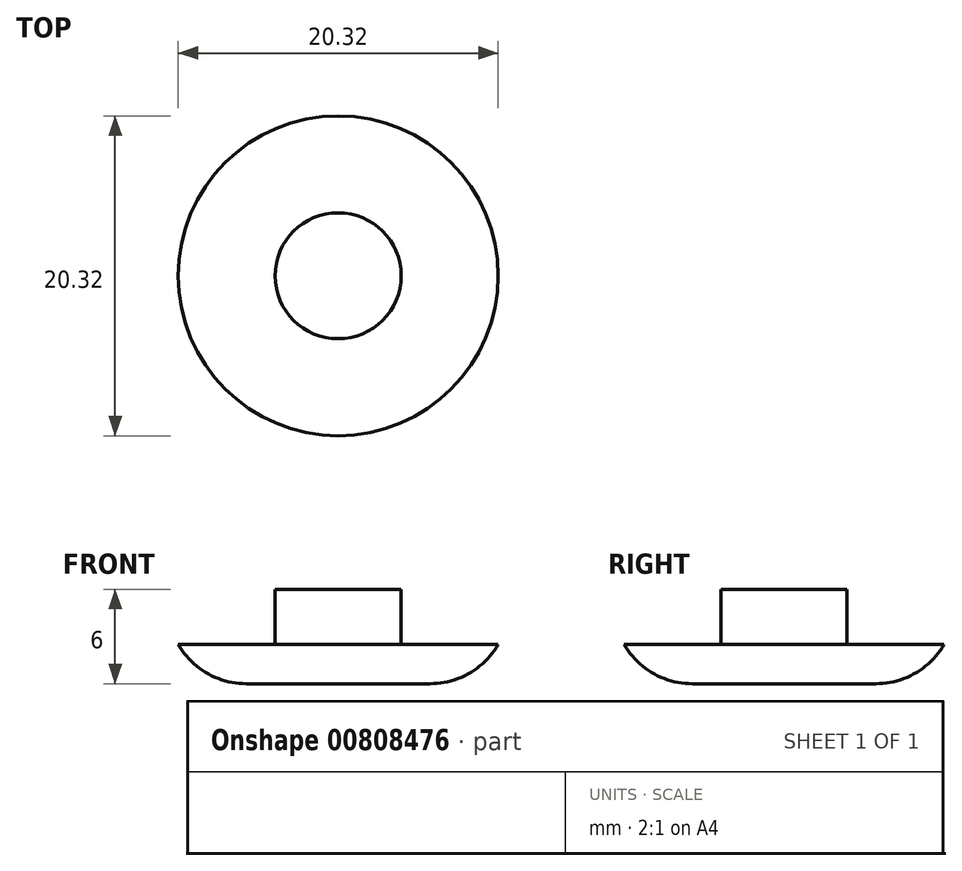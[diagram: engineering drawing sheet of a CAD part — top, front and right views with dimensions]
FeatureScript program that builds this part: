
annotation { "Feature Type Name" : "Feature", "Feature Type Description" : "" }
export const myFeature = defineFeature(function(context is Context, id is Id, definition is map)
    precondition{}
    {
        {
            var Q0;
            Q0=qCreatedBy(makeId("Top.planeOp"),FACE);
            var sketch = newSketch(context, id + "F0", { "sketchPlane" : qUnion([Q0])});
            skCircle(sketch, "E0", {"center": v(0, 0) * mm, "radius": 10.16 * mm});
            skSolve(sketch);
        }
        {
            var Q0;
            Q0 = qSketchRegion(id + "F0", true);
            extrude(context, id + "F1", {"entities" : qUnion([Q0]), "depth" : 2.5 * mm, "offsetDistance" : 25 * mm});
        }
        {
            var Q0;
            Q0=makeQuery(id+"F1.opExtrude","CAP_FACE",FACE,{"disambiguationData":[OSD([sQuery(id+"F0.wireOp",EDGE,"E0")])],"isStart":false});
            var sketch = newSketch(context, id + "F2", { "sketchPlane" : qUnion([Q0])});
            skCircle(sketch, "E1", {"center": v(0, 0) * mm, "radius": 4 * mm});
            skSolve(sketch);
        }
        {
            var Q0;
            Q0 = qSketchRegion(id + "F2", true);
            extrude(context, id + "F3", {"entities" : qUnion([Q0]), "operationType" : NewBodyOperationType.ADD, "depth" : 7 * mm / 2, "offsetDistance" : 25 * mm});
        }
        {
            var Q0;
            Q0=makeQuery(id+"F1.opExtrude","CAP_EDGE",EDGE,{"disambiguationData":[OSD([sQuery(id+"F0.wireOp",EDGE,"E0")])],"isStart":true});
            fillet(context, id + "F4", {"entities" : qUnion([Q0]), "radius" : 5 * mm, "tangentPropagation" : true, "allowEdgeOverflow" : false});
        }
        {
            var Q0;
            Q0=makeQuery(id+"F1.opExtrude","SWEPT_BODY",BODY,{"disambiguationData":[OSD([sQuery(id+"F0.wireOp",EDGE,"E0")])]});
            var Q1;
            Q1=qCreatedBy(makeId("Front.planeOp"),FACE);
            mirror(context, id + "F5", {"operationType" : NewBodyOperationType.ADD, "entities" : qUnion([Q0]), "mirrorPlane" : qUnion([Q1])});
        }
    });
